# Revit family: LEADER LED
name_source: partatom
category: Осветительные приборы
revit_build: Autodesk Revit 2016 (Build: 20150714_1515(x64)
units: mm (PartAtom-declared; Revit-internal decimal feet)

## family parameters
Источник света = Нет
Общий = Нет
Основа = Грань
При загрузке вырезать с полостями = Нет
Размер круглого соединителя = Использовать диаметр
Тип детали = Нормальный
Точка расчета площади = Нет

## types (1)
- LEADER LED
    ADSK_Единица измерения = Шт.
    ADSK_Завод-изготовитель = ООО МГК Световые технологии
    ADSK_Классификация нагрузок = Прочее
    ADSK_Код изделия = 1350000110
    ADSK_Количество фаз = 1
    ADSK_Количество фаз числовое = 1
    ADSK_Коэффициент мощности = 0.85
    ADSK_Масса = 9
    ADSK_Наименование = Серия светильников LEADER LED предназначена для архитектурного и функционального освещения. Дизайн светильника позволяет размещать его как на фасадах зданий, так и на промышленных площадках. Широкий выбор мощностей и оптических систем делает данный прожектор универсальным решением для самых сложных проектов наружного освещения
    ADSK_Напряжение = 230 В
    ADSK_Номинальная мощность = 0 кВт
    ADSK_Полная мощность = 0 кВ·А
    ADSK_Размер_Высота = 480 мм
    ADSK_Размер_Длина = 417 мм
    ADSK_Размер_Радиус = 10 мм
    ADSK_Размер_Ширина = 78 мм
    ADSK_Ток = 0 А
    ADSK_Энергоэффективность = 114 лм/Вт
    IP Class = IP66
    URL = https://www.ltcompany.com
    r = 1536 мм
    Блок аварийного питания = Нет
    Выбор ИС = IES_LEADER LED : 100 D15 3000K 12000
    Группа модели = Светильники
    Да = Нет
    Изготовитель = ООО МГК Световые технологии
    Класс Защиты = I
    Класс пожароопасности = П-I,II,IIa,ІІІ
    Климатическая зона = УХЛ1
    Код по классификатору = D5020200
    Корпус = Cерый металл матовый
    Нет = Нет
    Область использования = Автостоянки/парковки, Архитектурное освещение, Нефтегазовая промышленность, Освещение дорог, Открытые спортивные площадки
    Описание = Серия светильников LEADER LED предназначена для архитектурного и функционального освещения. Дизайн светильника позволяет размещать его как на фасадах зданий, так и на промышленных площадках. Широкий выбор мощностей и оптических систем делает данный прожектор универсальным решением для самых сложных проектов наружного освещения
    Ось.вращения = 192 мм
    Отметка по умолчанию = 0 мм
    Отступ1 = 48 мм
    Отступ2 = 185 мм
    Плафон = Плафон самосвечение
    Полная установленная мощность = 0 кВ·А
    Тип ИС = LED
    Тип ПРА = Драйвер
    Тип продукции = Светильник
